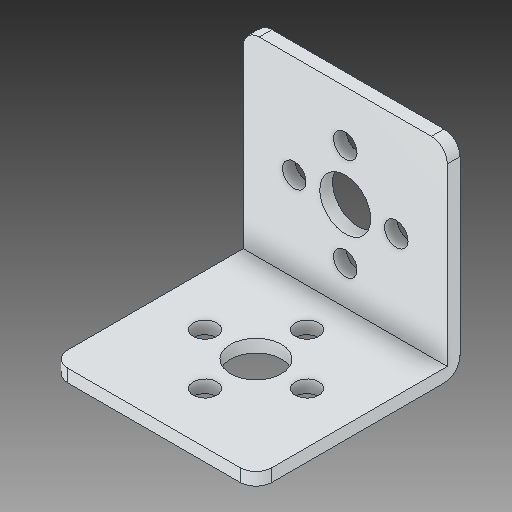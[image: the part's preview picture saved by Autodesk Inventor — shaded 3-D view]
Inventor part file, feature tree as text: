
AUTODESK INVENTOR PART (.ipt)
format: ipt  version: 2018 (Build 220112000, 112)  size: 162,304 bytes
history: native  units: in
note: dims shown in document units (in); Inventor stores cm internally (conversion verified against a paired STEP export)
features: fillet x1
ambient origin geometry x8: Origin, YZ Plane, XZ Plane, XY Plane, X Axis, Y Axis, Z Axis, Center Point
bodies: Solid1 (feature_tree)
feature tree (1):
  fillet  "Fillet1"  [1 undecoded]
note: 1 required parameter value undecoded (feature->parameter linkage not recoverable at this tier; creation-order binding heuristic only, values carry confidence <= 0.55)
